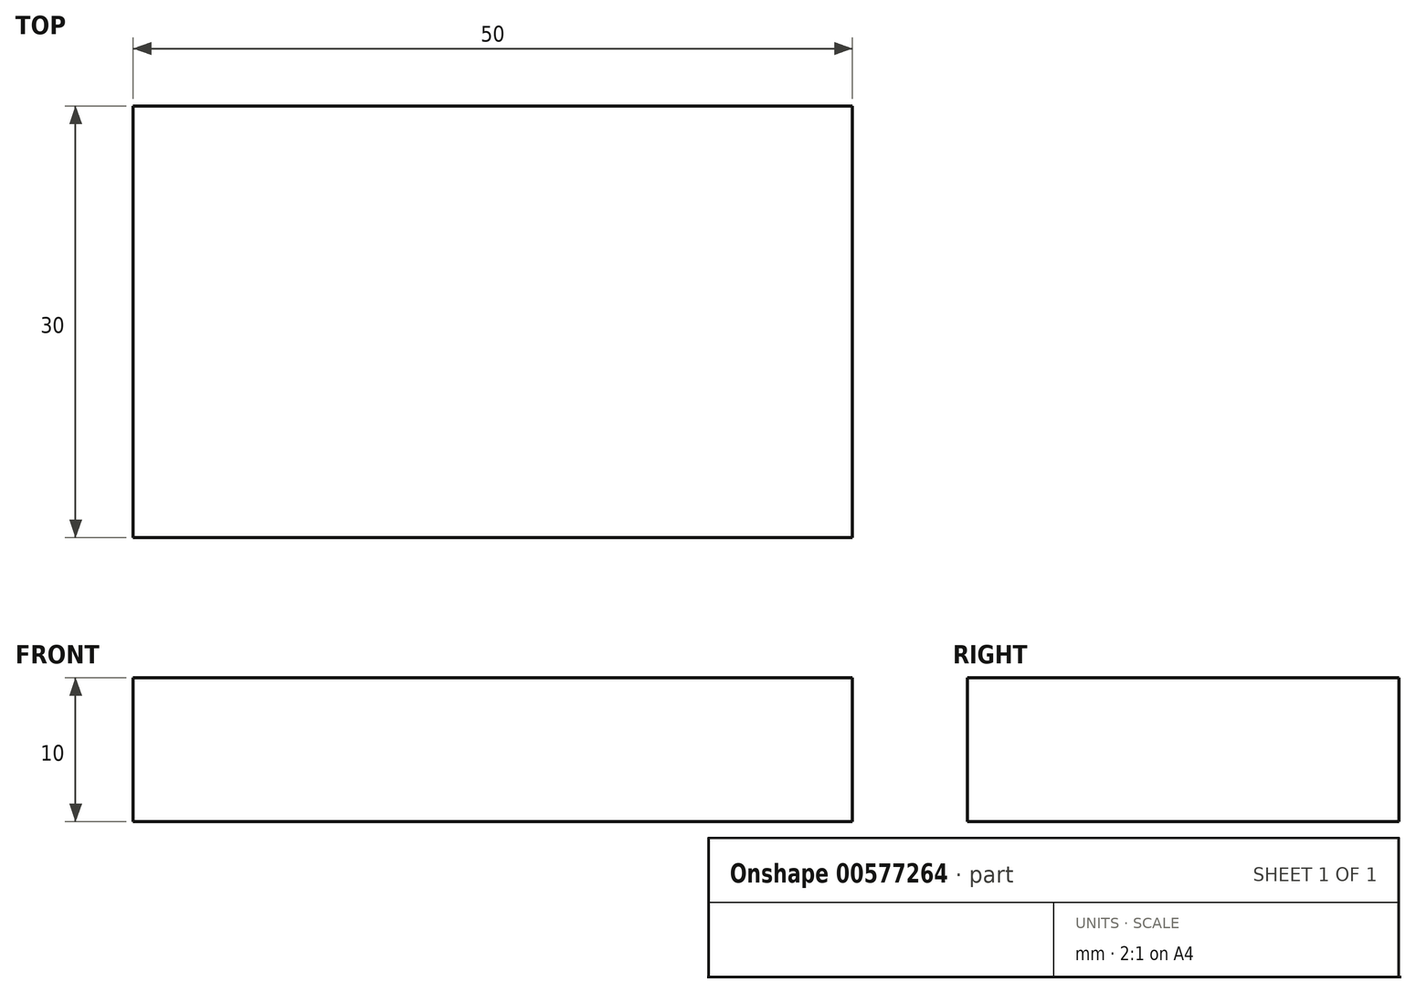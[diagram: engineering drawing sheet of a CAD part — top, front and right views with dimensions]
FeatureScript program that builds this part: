
annotation { "Feature Type Name" : "Feature", "Feature Type Description" : "" }
export const myFeature = defineFeature(function(context is Context, id is Id, definition is map)
    precondition{}
    {
        {
            var Q0;
            Q0=qCreatedBy(makeId("Top.planeOp"),FACE);
            var sketch = newSketch(context, id + "F0", { "sketchPlane" : qUnion([Q0])});
            skLineSegment(sketch, "E0.bottom", {"start": v(-21.64, 14.89) * mm, "end": v(28.36, 14.89) * mm});
            skLineSegment(sketch, "E0.top", {"start": v(-21.64, -15.11) * mm, "end": v(28.36, -15.11) * mm});
            skLineSegment(sketch, "E0.left", {"start": v(-21.64, 14.89) * mm, "end": v(-21.64, -15.11) * mm});
            skLineSegment(sketch, "E0.right", {"start": v(28.36, 14.89) * mm, "end": v(28.36, -15.11) * mm});
            skSolve(sketch);
        }
        {
            var Q0;
            Q0=makeQuery(id+"F0.imprint","IMPRINT",FACE,{"disambiguationData":[TD([[makeQuery(id+"F0.imprint","IMPRINT",EDGE,{"derivedFrom":sQuery(id+"F0.wireOp",EDGE,"E0.bottom")}),-1.0]])]});
            extrude(context, id + "F1", {"entities" : qUnion([Q0]), "depth" : 10 * mm, "offsetDistance" : 25 * mm});
        }
    });
